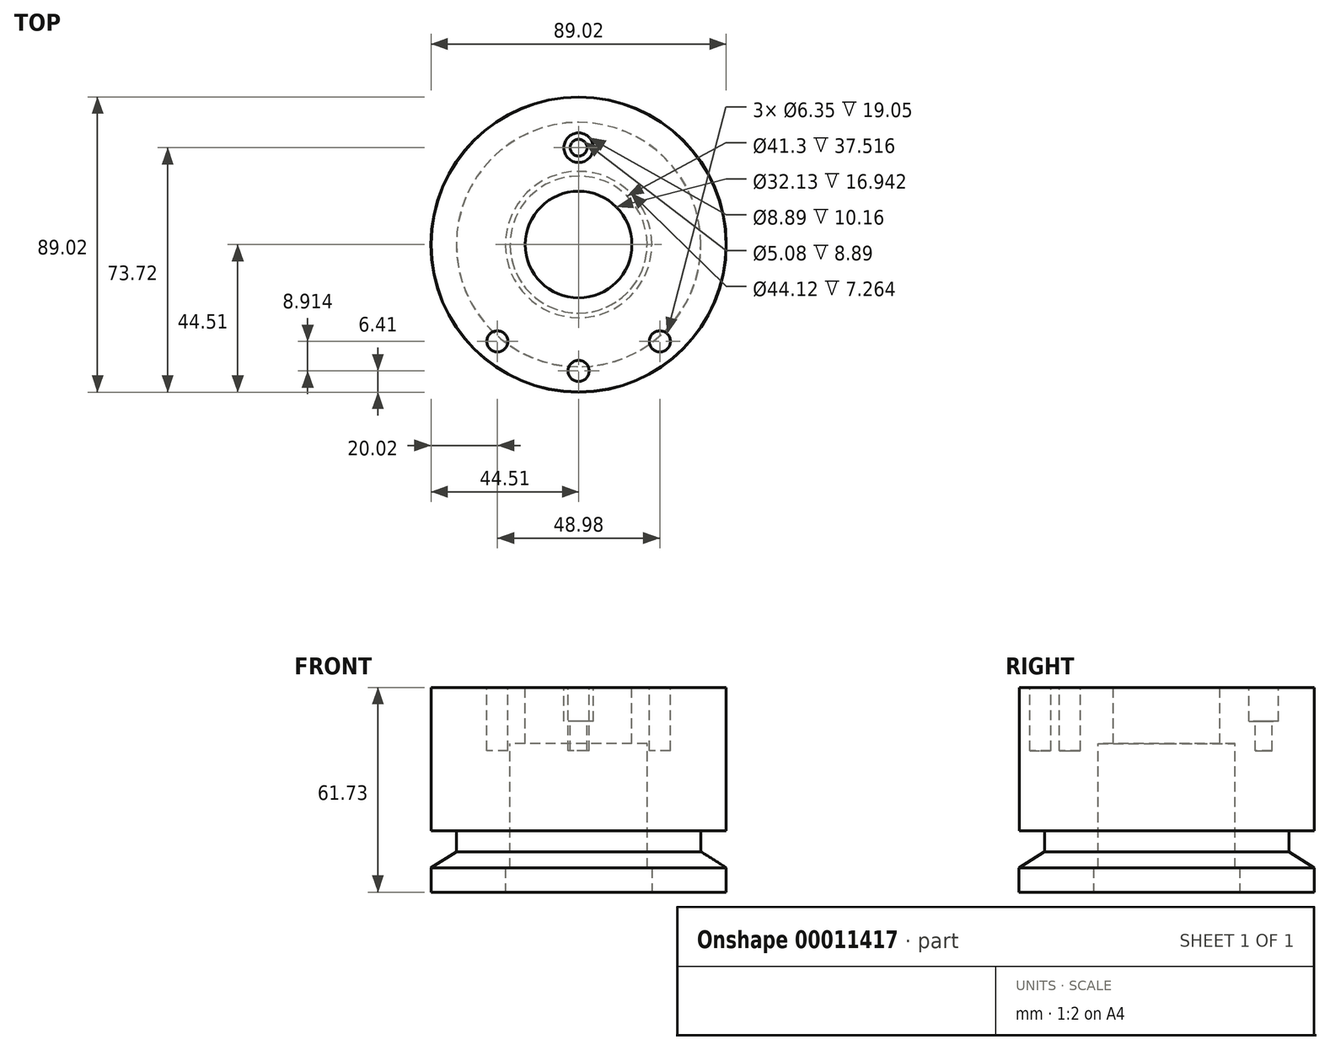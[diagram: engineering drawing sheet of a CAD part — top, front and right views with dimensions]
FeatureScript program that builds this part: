
annotation { "Feature Type Name" : "Feature", "Feature Type Description" : "" }
export const myFeature = defineFeature(function(context is Context, id is Id, definition is map)
    precondition{}
    {
        {
            var Q0;
            Q0=qCreatedBy(makeId("Front.planeOp"),FACE);
            var sketch = newSketch(context, id + "F0", { "sketchPlane" : qUnion([Q0])});
            skLineSegment(sketch, "E0", {"start": v(0, 0) * mm, "end": v(44.51, 0) * mm});
            skLineSegment(sketch, "E1", {"start": v(44.51, 0) * mm, "end": v(36.88, 4.83) * mm});
            skLineSegment(sketch, "E2", {"start": v(36.88, 4.83) * mm, "end": v(0, 4.83) * mm});
            skLineSegment(sketch, "E3", {"start": v(0, 4.83) * mm, "end": v(0, 0) * mm});
            skSolve(sketch);
        }
        {
            var Q0;
            Q0=makeQuery(id+"F0.imprint","IMPRINT",FACE,{"disambiguationData":[TD([[makeQuery(id+"F0.imprint","IMPRINT",EDGE,{"derivedFrom":sQuery(id+"F0.wireOp",EDGE,"E0")}),1.0]])]});
            var Q1;
            Q1=sQuery(id+"F0.wireOp",EDGE,"E3");
            revolve(context, id + "F1", {"entities" : qUnion([Q0]), "axis" : qUnion([Q1]), "revolveType" : RevolveType.FULL});
        }
        {
            var Q0;
            Q0=makeQuery(id+"F1.opRevolve","SWEPT_FACE",FACE,{"disambiguationData":[OSD([sQuery(id+"F0.wireOp",EDGE,"E0")])]});
            var sketch = newSketch(context, id + "F2", { "sketchPlane" : qUnion([Q0])});
            skCircle(sketch, "E4", {"center": v(0, 0) * mm, "radius": 44.5 * mm});
            skSolve(sketch);
        }
        {
            var Q0;
            Q0 = qSketchRegion(id + "F2", true);
            extrude(context, id + "F3", {"entities" : qUnion([Q0]), "operationType" : NewBodyOperationType.ADD, "depth" : 7.37 * mm});
        }
        {
            var Q0;
            Q0=makeQuery(id+"F1.opRevolve","SWEPT_FACE",FACE,{"disambiguationData":[OSD([sQuery(id+"F0.wireOp",EDGE,"E2")])]});
            var sketch = newSketch(context, id + "F4", { "sketchPlane" : qUnion([Q0])});
            skCircle(sketch, "E5", {"center": v(0, 0) * mm, "radius": 36.83 * mm});
            skSolve(sketch);
        }
        {
            var Q0;
            Q0 = qSketchRegion(id + "F4", true);
            extrude(context, id + "F5", {"entities" : qUnion([Q0]), "operationType" : NewBodyOperationType.ADD, "depth" : 6.35 * mm});
        }
        {
            var Q0;
            Q0=makeQuery(id+"F5.opExtrude","CAP_FACE",FACE,{"disambiguationData":[OSD([sQuery(id+"F4.wireOp",EDGE,"E5")])],"isStart":false});
            var sketch = newSketch(context, id + "F6", { "sketchPlane" : qUnion([Q0])});
            skCircle(sketch, "E6", {"center": v(0, 0) * mm, "radius": 44.45 * mm});
            skSolve(sketch);
        }
        {
            var Q0;
            Q0 = qSketchRegion(id + "F6", true);
            var Q1;
            Q1 = qSketchRegion(id + "F8", true);
            extrude(context, id + "F7", {"entities" : qUnion([Q0, Q1]), "operationType" : NewBodyOperationType.ADD, "depth" : 43.18 * mm});
        }
        {
            var Q0;
            Q0=makeQuery(id+"F7.opExtrude","CAP_FACE",FACE,{"disambiguationData":[OSD([sQuery(id+"F6.wireOp",EDGE,"E6")])],"isStart":false});
            var sketch = newSketch(context, id + "F8", { "sketchPlane" : qUnion([Q0])});
            skCircle(sketch, "E7", {"center": v(0, 0) * mm, "radius": 16.07 * mm});
            skSolve(sketch);
        }
        {
            var Q0;
            Q0 = qSketchRegion(id + "F8", true);
            extrude(context, id + "F9", {"entities" : qUnion([Q0]), "operationType" : NewBodyOperationType.REMOVE, "oppositeDirection" : true, "depth" : 16.94 * mm});
        }
        {
            var Q0;
            Q0=makeQuery(id+"F9.boolean.opBoolean","COPY",FACE,{"derivedFrom":makeQuery(id+"F9.opExtrude","CAP_FACE",FACE,{"disambiguationData":[OSD([sQuery(id+"F8.wireOp",EDGE,"E7")])],"isStart":false})});
            var sketch = newSketch(context, id + "F10", { "sketchPlane" : qUnion([Q0])});
            skCircle(sketch, "E8", {"center": v(0, 0) * mm, "radius": 20.65 * mm});
            skSolve(sketch);
        }
        {
            var Q0;
            Q0 = qSketchRegion(id + "F10", true);
            var Q1;
            Q1 = qSketchRegion(id + "F12", true);
            var Q2;
            Q2=makeQuery(id+"F3.opExtrude","CAP_FACE",FACE,{"disambiguationData":[OSD([sQuery(id+"F2.wireOp",EDGE,"E4")])],"isStart":false});
            extrude(context, id + "F11", {"entities" : qUnion([Q0, Q1]), "operationType" : NewBodyOperationType.REMOVE, "endBound" : BoundingType.UP_TO_SURFACE, "oppositeDirection" : true, "endBoundEntityFace" : qUnion([Q2]), "depth" : 25.4 * mm});
        }
        {
            var Q0;
            Q0=makeQuery(id+"F7.opExtrude","CAP_FACE",FACE,{"disambiguationData":[OSD([sQuery(id+"F6.wireOp",EDGE,"E6")])],"isStart":false});
            var sketch = newSketch(context, id + "F12", { "sketchPlane" : qUnion([Q0])});
            skCircle(sketch, "E9", {"center": v(0, 29.21) * mm, "radius": 2.54 * mm});
            skCircle(sketch, "E10", {"center": v(0, 0) * mm, "radius": 38.1 * mm, "construction": true});
            skCircle(sketch, "E11", {"center": v(0, -38.1) * mm, "radius": 3.18 * mm});
            skCircle(sketch, "E12.1.0", {"center": v(24.5, -29.19) * mm, "radius": 3.18 * mm});
            skCircle(sketch, "E12.8.0", {"center": v(-24.5, -29.19) * mm, "radius": 3.18 * mm});
            skSolve(sketch);
        }
        {
            var Q0;
            Q0 = qSketchRegion(id + "F12", true);
            extrude(context, id + "F13", {"entities" : qUnion([Q0]), "operationType" : NewBodyOperationType.REMOVE, "oppositeDirection" : true, "depth" : 19.05 * mm});
        }
        {
            var Q0;
            Q0=makeQuery(id+"F7.opExtrude","CAP_FACE",FACE,{"disambiguationData":[OSD([sQuery(id+"F6.wireOp",EDGE,"E6")])],"isStart":false});
            var sketch = newSketch(context, id + "F14", { "sketchPlane" : qUnion([Q0])});
            skCircle(sketch, "E13", {"center": v(0, 29.21) * mm, "radius": 4.45 * mm});
            skSolve(sketch);
        }
        {
            var Q0;
            Q0 = qSketchRegion(id + "F14", true);
            extrude(context, id + "F15", {"entities" : qUnion([Q0]), "operationType" : NewBodyOperationType.REMOVE, "oppositeDirection" : true, "depth" : 10.16 * mm});
        }
        {
            var Q0;
            Q0=makeQuery(id+"F3.opExtrude","CAP_FACE",FACE,{"disambiguationData":[OSD([sQuery(id+"F2.wireOp",EDGE,"E4")])],"isStart":false});
            var sketch = newSketch(context, id + "F16", { "sketchPlane" : qUnion([Q0])});
            skCircle(sketch, "E14", {"center": v(0, 0) * mm, "radius": 22.06 * mm});
            skSolve(sketch);
        }
        {
            var Q0;
            Q0 = qSketchRegion(id + "F16", true);
            extrude(context, id + "F17", {"entities" : qUnion([Q0]), "operationType" : NewBodyOperationType.REMOVE, "oppositeDirection" : true, "depth" : 7.26 * mm});
        }
    });
